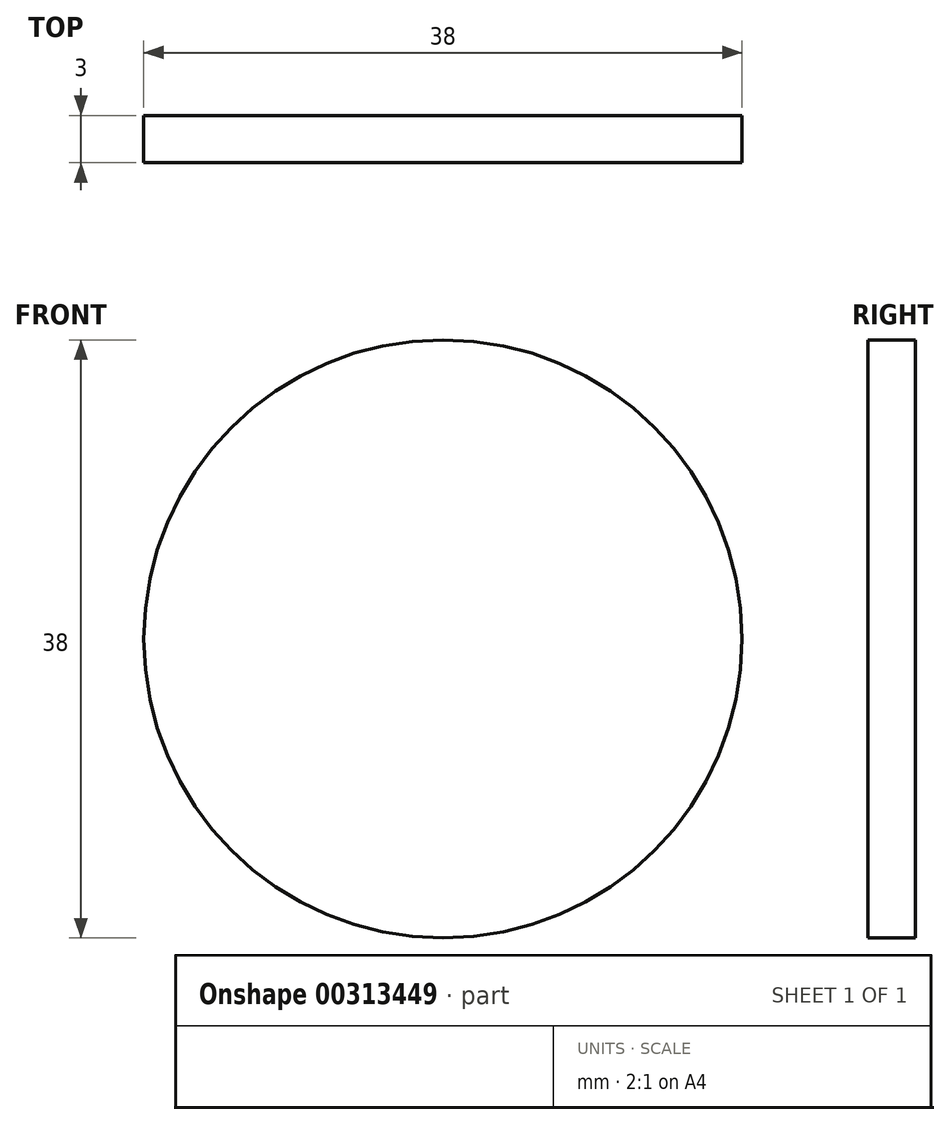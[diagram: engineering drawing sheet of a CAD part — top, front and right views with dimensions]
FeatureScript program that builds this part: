
annotation { "Feature Type Name" : "Feature", "Feature Type Description" : "" }
export const myFeature = defineFeature(function(context is Context, id is Id, definition is map)
    precondition{}
    {
        {
            var Q0;
            Q0=qCreatedBy(makeId("Front.planeOp"),FACE);
            var sketch = newSketch(context, id + "F0", { "sketchPlane" : qUnion([Q0])});
            skCircle(sketch, "E0", {"center": v(0, 0) * mm, "radius": 19 * mm});
            skSolve(sketch);
        }
        {
            var Q0;
            Q0=makeQuery(id+"F0.imprint","IMPRINT",FACE,{"disambiguationData":[TD([[makeQuery(id+"F0.imprint","IMPRINT",EDGE,{"derivedFrom":sQuery(id+"F0.wireOp",EDGE,"E0")}),1.0]])]});
            extrude(context, id + "F1", {"entities" : qUnion([Q0]), "depth" : 3 * mm});
        }
    });
